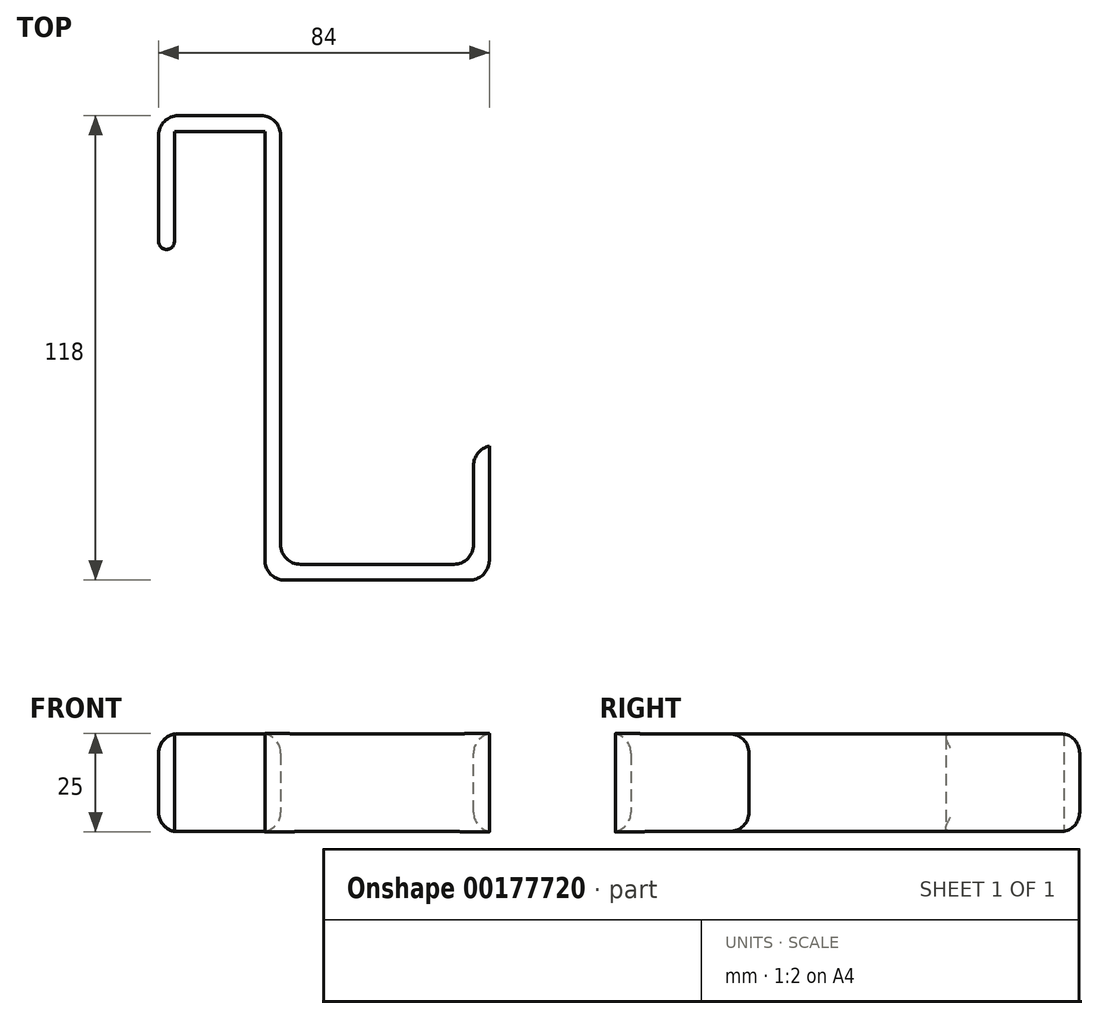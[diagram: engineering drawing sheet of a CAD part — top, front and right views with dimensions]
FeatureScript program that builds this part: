
annotation { "Feature Type Name" : "Feature", "Feature Type Description" : "" }
export const myFeature = defineFeature(function(context is Context, id is Id, definition is map)
    precondition{}
    {
        {
            var Q0;
            Q0=qCreatedBy(makeId("Top.planeOp"),FACE);
            var sketch = newSketch(context, id + "F0", { "sketchPlane" : qUnion([Q0])});
            skLineSegment(sketch, "E0", {"start": v(-39.5, 35.13) * mm, "end": v(-39.5, 65.13) * mm});
            skLineSegment(sketch, "E1", {"start": v(-39.5, 65.13) * mm, "end": v(-16.5, 65.13) * mm});
            skLineSegment(sketch, "E2", {"start": v(-12.5, 65.13) * mm, "end": v(-12.5, -44.87) * mm});
            skLineSegment(sketch, "E3", {"start": v(-12.5, -44.87) * mm, "end": v(36.5, -44.87) * mm});
            skLineSegment(sketch, "E4", {"start": v(36.5, -44.87) * mm, "end": v(36.5, -14.87) * mm});
            skLineSegment(sketch, "E5.0", {"start": v(-43.5, 69.13) * mm, "end": v(-12.5, 69.13) * mm});
            skLineSegment(sketch, "E5.1", {"start": v(-43.5, 35.13) * mm, "end": v(-43.5, 69.13) * mm});
            skLineSegment(sketch, "E6.0", {"start": v(-16.5, 65.13) * mm, "end": v(-16.5, -44.87) * mm});
            skLineSegment(sketch, "E7.0", {"start": v(-13.5, -48.87) * mm, "end": v(36.5, -48.87) * mm});
            skLineSegment(sketch, "E8.0", {"start": v(40.5, -44.87) * mm, "end": v(40.5, -14.87) * mm});
            skLineSegment(sketch, "E9", {"start": v(-39.5, 35.13) * mm, "end": v(-43.5, 35.13) * mm});
            skLineSegment(sketch, "E10", {"start": v(-12.5, 65.13) * mm, "end": v(-12.5, 69.13) * mm});
            skLineSegment(sketch, "E11", {"start": v(36.5, -14.87) * mm, "end": v(40.5, -14.87) * mm});
            skLineSegment(sketch, "E12", {"start": v(40.5, -44.87) * mm, "end": v(40.5, -48.79) * mm});
            skLineSegment(sketch, "E13", {"start": v(36.5, -48.87) * mm, "end": v(40.5, -48.79) * mm});
            skPoint(sketch, "E13.endSnap0", {"position": v(40.5, -48.67) * mm});
            skLineSegment(sketch, "E14", {"start": v(-16.5, -44.87) * mm, "end": v(-16.5, -48.87) * mm});
            skLineSegment(sketch, "E15", {"start": v(-13.5, -48.87) * mm, "end": v(-16.5, -48.87) * mm});
            skSolve(sketch);
        }
        {
            var Q0;
            Q0 = qSketchRegion(id + "F0", true);
            extrude(context, id + "F1", {"entities" : qUnion([Q0]), "depth" : 25 * mm});
        }
        {
            var Q0;
            Q0=makeQuery(id+"F1.opExtrude","SWEPT_EDGE",EDGE,{"disambiguationData":[OSD([sQuery(id+"F0.wireOp",EDGE,"E14"),sQuery(id+"F0.wireOp",EDGE,"E15")])]});
            var Q1;
            Q1=makeQuery(id+"F1.opExtrude","SWEPT_EDGE",EDGE,{"disambiguationData":[OSD([sQuery(id+"F0.wireOp",EDGE,"E12"),sQuery(id+"F0.wireOp",EDGE,"E13")])]});
            var Q2;
            Q2=makeQuery(id+"F1.opExtrude","SWEPT_EDGE",EDGE,{"disambiguationData":[OSD([sQuery(id+"F0.wireOp",EDGE,"E4"),sQuery(id+"F0.wireOp",EDGE,"E11")])]});
            var Q3;
            Q3=makeQuery(id+"F1.opExtrude","SWEPT_EDGE",EDGE,{"disambiguationData":[OSD([sQuery(id+"F0.wireOp",EDGE,"E5.0"),sQuery(id+"F0.wireOp",EDGE,"E10")])]});
            var Q4;
            Q4=makeQuery(id+"F1.opExtrude","SWEPT_EDGE",EDGE,{"disambiguationData":[OSD([sQuery(id+"F0.wireOp",EDGE,"E2"),sQuery(id+"F0.wireOp",EDGE,"E3")])]});
            var Q5;
            Q5=makeQuery(id+"F1.opExtrude","SWEPT_EDGE",EDGE,{"disambiguationData":[OSD([sQuery(id+"F0.wireOp",EDGE,"E3"),sQuery(id+"F0.wireOp",EDGE,"E4")])]});
            var Q6;
            Q6=makeQuery(id+"F1.opExtrude","SWEPT_EDGE",EDGE,{"disambiguationData":[OSD([sQuery(id+"F0.wireOp",EDGE,"E5.0"),sQuery(id+"F0.wireOp",EDGE,"E5.1")])]});
            fillet(context, id + "F2", {"entities" : qUnion([Q0, Q1, Q2, Q3, Q4, Q5, Q6]), "radius" : 5 * mm, "tangentPropagation" : true, "allowEdgeOverflow" : false});
        }
        {
            var Q0;
            Q0=makeQuery(id+"F1.opExtrude","SWEPT_EDGE",EDGE,{"disambiguationData":[OSD([sQuery(id+"F0.wireOp",EDGE,"E5.1"),sQuery(id+"F0.wireOp",EDGE,"E9")])]});
            var Q1;
            Q1=makeQuery(id+"F1.opExtrude","SWEPT_EDGE",EDGE,{"disambiguationData":[OSD([sQuery(id+"F0.wireOp",EDGE,"E0"),sQuery(id+"F0.wireOp",EDGE,"E9")])]});
            fillet(context, id + "F3", {"entities" : qUnion([Q0, Q1]), "radius" : 2 * mm, "tangentPropagation" : true, "allowEdgeOverflow" : false});
        }
        {
            var Q0;
            Q0=makeQuery(id+"F1.opExtrude","CAP_EDGE",EDGE,{"disambiguationData":[OSD([sQuery(id+"F0.wireOp",EDGE,"E2"),sQuery(id+"F0.wireOp",EDGE,"E10")])],"isStart":false});
            var Q1;
            Q1=makeQuery(id+"F1.opExtrude","CAP_EDGE",EDGE,{"disambiguationData":[OSD([sQuery(id+"F0.wireOp",EDGE,"E2"),sQuery(id+"F0.wireOp",EDGE,"E10")])],"isStart":true});
            fillet(context, id + "F4", {"entities" : qUnion([Q0, Q1]), "radius" : 5 * mm, "tangentPropagation" : true, "allowEdgeOverflow" : false});
        }
    });
